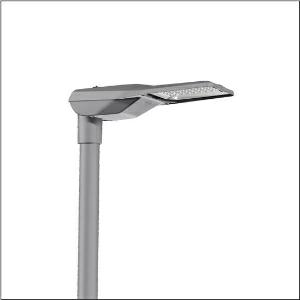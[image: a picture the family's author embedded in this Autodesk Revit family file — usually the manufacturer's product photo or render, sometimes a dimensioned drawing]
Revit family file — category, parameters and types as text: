
# Revit family: streetlight_sl_21_iq_mini___st1_0a_5xe2d31v08jb_ee78
name_source: partatom
category: Lighting Fixtures
units: mm (PartAtom-declared; Revit-internal decimal feet)

## family parameters
Cut with Voids When Loaded = No
Host = Face
Light Source = No
Part Type = Normal
Room Calculation Point = No
Round Connector Dimension = Use Diameter
Shared = No

## types (1)
- --- (1 x LED, 11210 lm, 72.5 W, 3000K)
    Apparent Load = 73 VA
    CIE Flux Codes = 40 73 97 100 100
    Color Rendering = 70
    Color Temperature = 3000K
    Default Elevation = 1800 mm
    Description = Streetlight SL 21 iQ mini, mast luminaire, primary light control with lens, of PMMA, primary optical cover: cover, of toughened safety glass, transparent, light distribution: ST1.0a, light emission: direct distribution, primary light characteristic: asymmetric, installation type: post-top, side-entry, LED, High Power LED, rated luminous flux: 11.210lm, luminous efficacy: 155lm/W, light colour: 730, colour temperature: 3000K, control: presetting dimming logarithmic, Street-Remote, Auto-Match, Temp-Guard, Lumen-Switch, Night-Set, Smart-Wire, Light-Fading, Desk-Remote (wireless, voltage-free reading and setting of iQ features in the workshop via application-optimized NFC function/RFID function), optimised constant luminous flux control (CLO 2.0), mains connection: 220..240V, AC, 50/60Hz, start of lifetime: 73W, end of service life: 76W, reduction: 33W, luminaire housing, of diecast aluminium, powder-coated, Siteco® metallic grey (DB 702S), corrosivity category C5 mid according to DIN EN ISO 12944, please order mast flange separately, inclination adjustable: 0°, 5°, 10°, 15°, sealing non-destructively replaceable, multi-level sealing system, length: 628mm, width: 235mm, height: 110mm, mast flange for spigot size: 42mm (side-entry): 5XC10008XM4, 60/48mm (side-entry/post-top): 5XC10108XM2, 76/60mm (side-entry/post-top): 5XC10108XM1, Smart Interface above, protection rating (complete): IP66, insulation class (complete): insulation class II (safety insulation), certification: CE, ENEC, ENEC+, VDE, impact resistance: IK09, permissible operating ambient temperature for outdoor applications: -40..+50°C, standard-compliant lighting for roads and squares, packaging unit: 1 piece

Light Distribution: ST1.0a
    Height = 110 mm
    Lamp = 1 x LED
    Lamp Light Flux = 11210 lm
    Lamp Power = 72.5 W
    Lamp count = 1
    Length = 625 mm
    Luminous efficacy = 155 lm/W
    Manufacturer = Siteco
    ModVariant = No
    Model = 5XE2D31V08JB
    Number of Poles = 1
    OnlyDefault = Yes
    Power Factor = 1
    Product Name = Streetlight SL 21 iQ mini | ST1.0a
    Product group = mast luminaire | pylon top
    ProductGroupID = 6100
    Protection Class = Protection class II
    Protection Degree = IP 66
    RLX_Detail_Level = 1
    RLX_Emergency_Light_Flux = 0 lm
    RLX_Emergency_Type = 0
    RLX_Emergency_Type_DB = No
    RlxData = <blob elided: 93309 chars, md5=81d38a2b>
    Socket = socket
    Standby Power = 0 W
    System Light Flux = 11210 lm
    System Power = 73 W
    Type Comments = factory setting: luminous flux: 100 % | dim-lin: 254 | 755 mA
    Type Image = l_1003515.jpg
    URL = http://relux.com
    VarID = @adj_062383
    Voltage = 0 V
    Weight = 0.00 kg
    Width = 234 mm

## geometry (parser evidence)
native form markers: Blend x4, Sweep x12
no freeform markers — native parametric forms only
